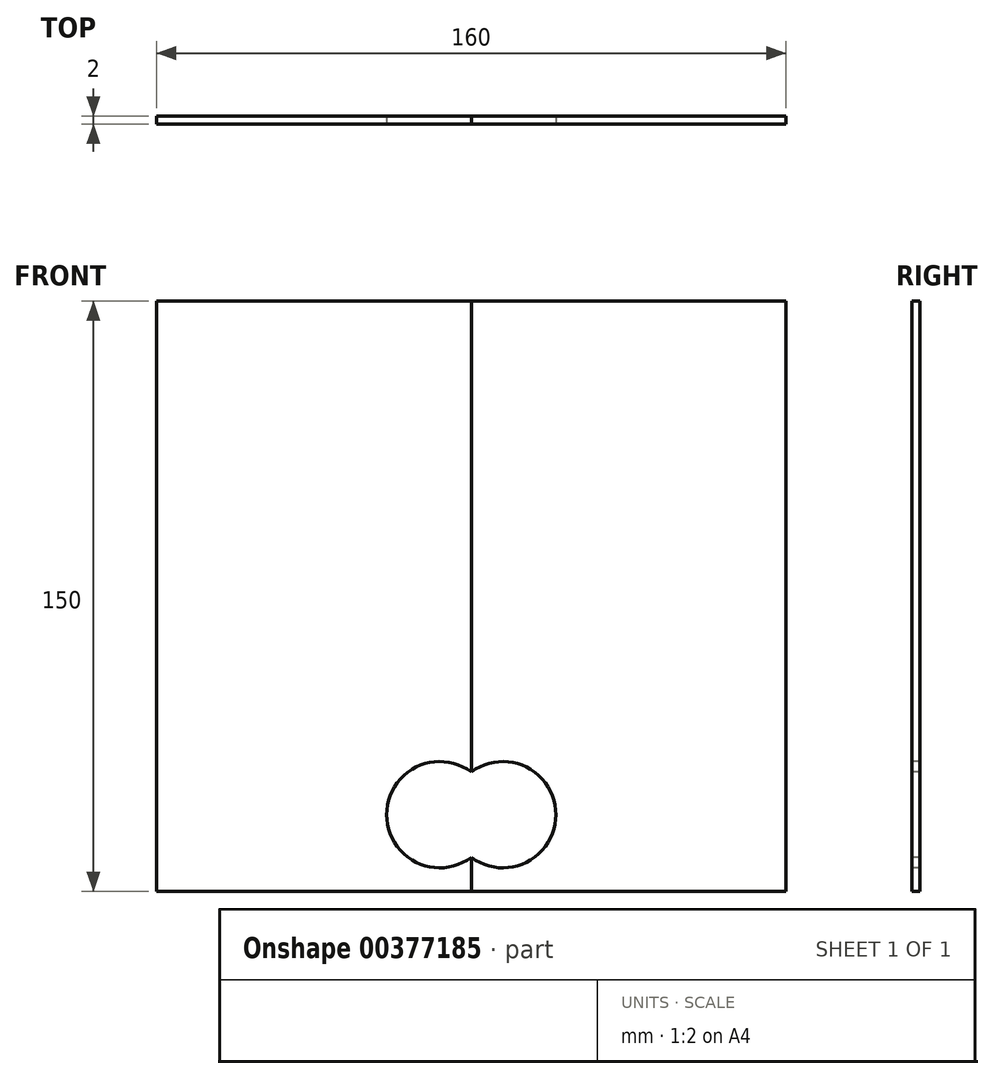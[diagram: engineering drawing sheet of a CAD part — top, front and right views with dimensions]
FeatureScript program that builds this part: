
annotation { "Feature Type Name" : "Feature", "Feature Type Description" : "" }
export const myFeature = defineFeature(function(context is Context, id is Id, definition is map)
    precondition{}
    {
        {
            var Q0;
            Q0=qCreatedBy(makeId("Front.planeOp"),FACE);
            var sketch = newSketch(context, id + "F0", { "sketchPlane" : qUnion([Q0])});
            skLineSegment(sketch, "E0", {"start": v(80, 0) * mm, "end": v(0, 0) * mm});
            skLineSegment(sketch, "E1", {"start": v(0, 0) * mm, "end": v(0, 150) * mm});
            skCircle(sketch, "E2", {"center": v(8, 19.5) * mm, "radius": 13.5 * mm});
            skLineSegment(sketch, "E3", {"start": v(0, 150) * mm, "end": v(80, 150) * mm});
            skLineSegment(sketch, "E4", {"start": v(80, 150) * mm, "end": v(80, 0) * mm});
            skSolve(sketch);
        }
        {
            var Q0;
            {var subQ1=sQuery(id+"F0.wireOp",EDGE,"QWGNVXtH-k0zN-P6z4-YVwU-eIhSdeUkkeIk");Q0=makeQuery(id+"F0.imprint","IMPRINT",FACE,{"disambiguationData":[TD([[makeQuery(id+"F0.imprint","IMPRINT",EDGE,{"derivedFrom":subQ1}),-1.0]])]});}
            var Q1;
            {var subQ0=sQuery(id+"F0.wireOp",EDGE,"E3");Q1=makeQuery(id+"F0.imprint","IMPRINT",FACE,{"disambiguationData":[TD([[makeQuery(id+"F0.imprint","IMPRINT",EDGE,{"derivedFrom":subQ0}),-1.0]])]});}
            extrude(context, id + "F1", {"entities" : qUnion([Q0, Q1]), "oppositeDirection" : true, "depth" : 2 * mm});
        }
        {
            var Q0;
            Q0=makeQuery(id+"F1.opExtrude","SWEPT_BODY",BODY,{"disambiguationData":[OSD([sQuery(id+"F0.wireOp",EDGE,"QWGNVXtH-k0zN-P6z4-YVwU-eIhSdeUkkeIk"),sQuery(id+"F0.wireOp",EDGE,"E0"),sQuery(id+"F0.wireOp",EDGE,"E1"),sQuery(id+"F0.wireOp",EDGE,"E2")])]});
            var Q1;
            Q1=qCreatedBy(makeId("Right.planeOp"),FACE);
            mirror(context, id + "F2", {"entities" : qUnion([Q0]), "mirrorPlane" : qUnion([Q1])});
        }
    });
